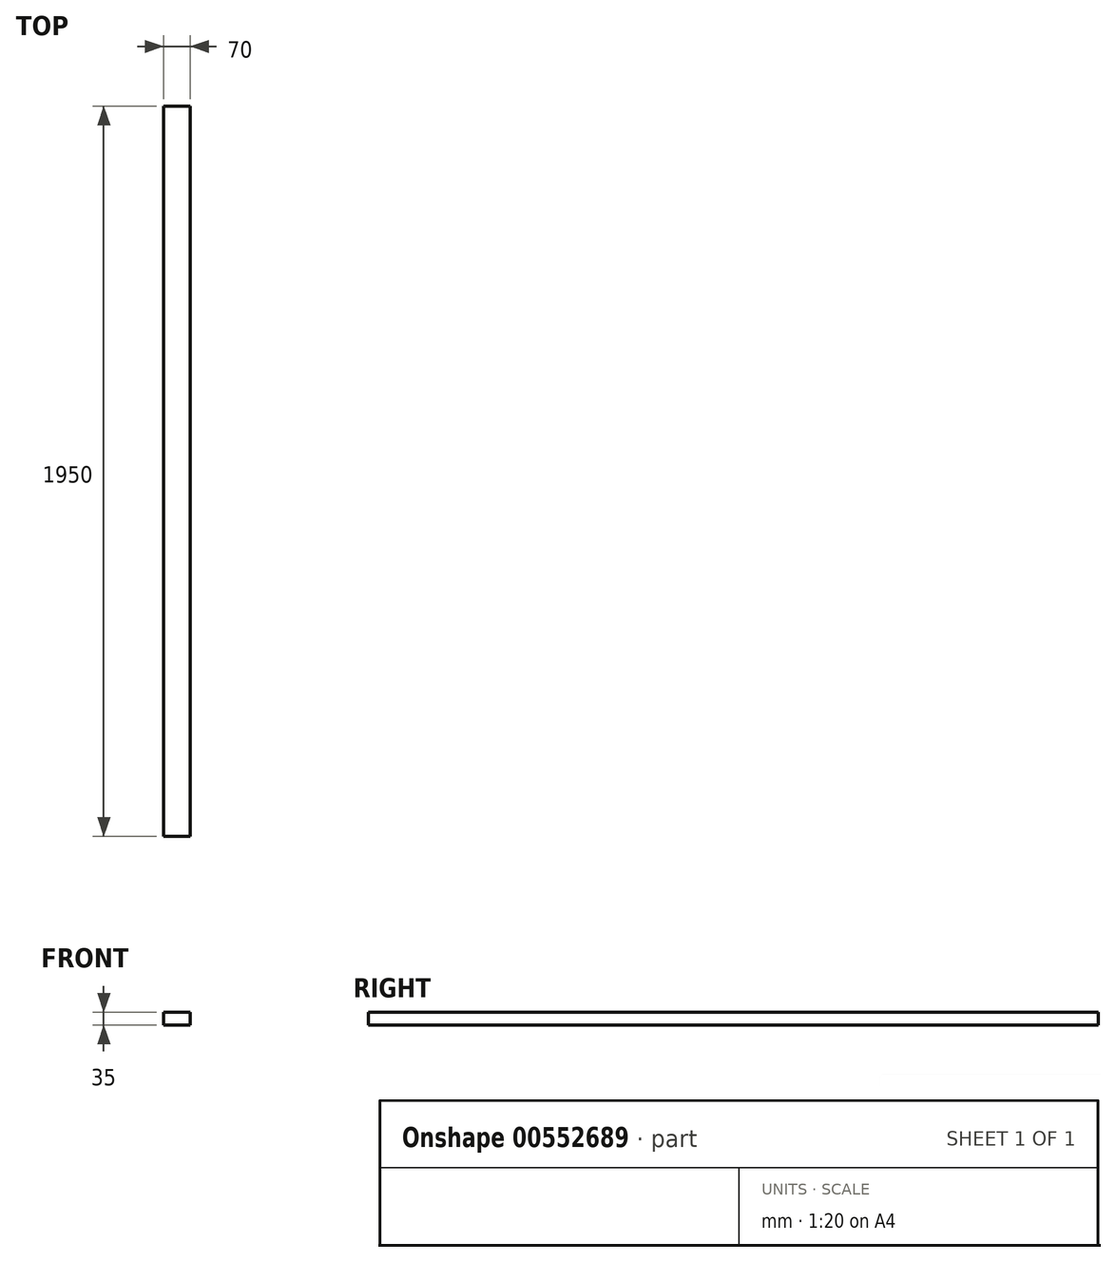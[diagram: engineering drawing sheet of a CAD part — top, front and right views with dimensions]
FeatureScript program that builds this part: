
annotation { "Feature Type Name" : "Feature", "Feature Type Description" : "" }
export const myFeature = defineFeature(function(context is Context, id is Id, definition is map)
    precondition{}
    {
        {
            var Q0;
            Q0=qCreatedBy(makeId("Front.planeOp"),FACE);
            var sketch = newSketch(context, id + "F0", { "sketchPlane" : qUnion([Q0])});
            skLineSegment(sketch, "E0.bottom", {"start": v(35, 17.5) * mm, "end": v(-35, 17.5) * mm});
            skLineSegment(sketch, "E0.top", {"start": v(35, -17.5) * mm, "end": v(-35, -17.5) * mm});
            skLineSegment(sketch, "E0.left", {"start": v(35, 17.5) * mm, "end": v(35, -17.5) * mm});
            skLineSegment(sketch, "E0.right", {"start": v(-35, 17.5) * mm, "end": v(-35, -17.5) * mm});
            skPoint(sketch, "E0.middle", {"position": v(0, 0) * mm});
            skSolve(sketch);
        }
        {
            var Q0;
            Q0 = qSketchRegion(id + "F0", true);
            extrude(context, id + "F1", {"entities" : qUnion([Q0]), "oppositeDirection" : true, "depth" : 1950 * mm, "offsetDistance" : 25 * mm});
        }
    });
